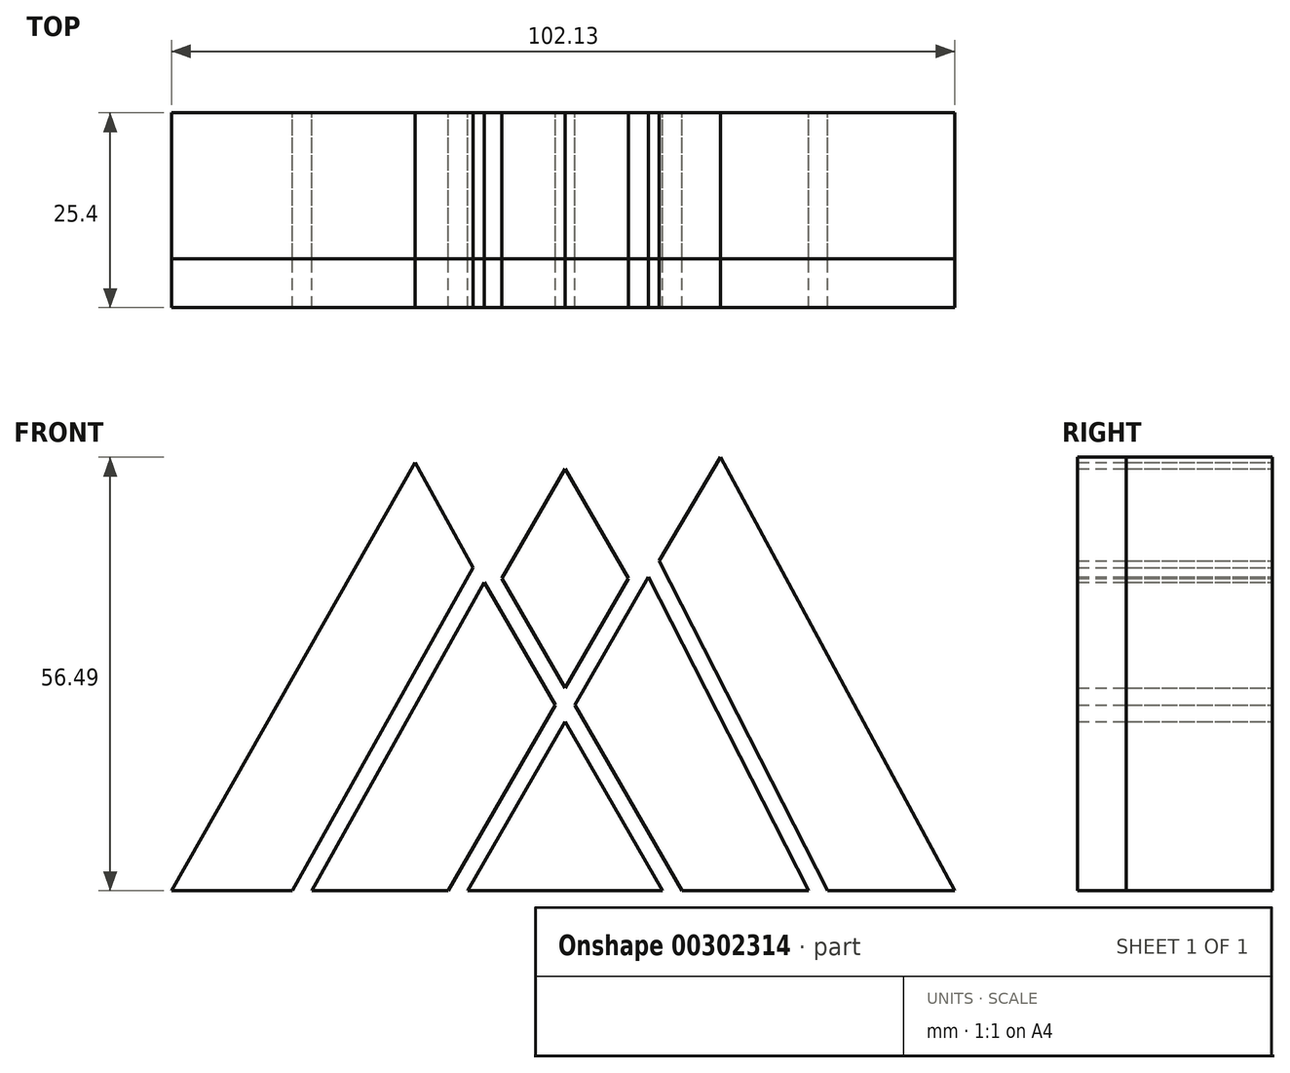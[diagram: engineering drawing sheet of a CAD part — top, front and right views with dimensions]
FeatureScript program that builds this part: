
annotation { "Feature Type Name" : "Feature", "Feature Type Description" : "" }
export const myFeature = defineFeature(function(context is Context, id is Id, definition is map)
    precondition{}
    {
        {
            var Q0;
            Q0=qCreatedBy(makeId("Front.planeOp"),FACE);
            var sketch = newSketch(context, id + "F0", { "sketchPlane" : qUnion([Q0])});
            skLineSegment(sketch, "E0", {"start": v(0, 0) * mm, "end": v(-12.7, -22) * mm});
            skLineSegment(sketch, "E1", {"start": v(0, 0) * mm, "end": v(12.7, -22) * mm});
            skLineSegment(sketch, "E2", {"start": v(-12.7, -22) * mm, "end": v(12.7, -22) * mm});
            skLineSegment(sketch, "E3", {"start": v(0, -22) * mm, "end": v(0, 0) * mm});
            skLineSegment(sketch, "E4", {"start": v(-19.53, 33.84) * mm, "end": v(-51.28, -22) * mm});
            skLineSegment(sketch, "E5", {"start": v(20.27, 34.5) * mm, "end": v(50.85, -22) * mm});
            skLineSegment(sketch, "E6", {"start": v(-11.95, 20.1) * mm, "end": v(-35.53, -22) * mm});
            skLineSegment(sketch, "E7", {"start": v(12.3, 21) * mm, "end": v(34.23, -22) * mm});
            skLineSegment(sketch, "E8", {"start": v(-1.27, 2.2) * mm, "end": v(-15.24, -22) * mm});
            skLineSegment(sketch, "E9", {"start": v(1.27, 2.2) * mm, "end": v(15.24, -22) * mm});
            skLineSegment(sketch, "E10", {"start": v(15.24, -22) * mm, "end": v(31.75, -22) * mm});
            skLineSegment(sketch, "E11", {"start": v(0, 33) * mm, "end": v(-8.26, 18.7) * mm});
            skLineSegment(sketch, "E12", {"start": v(-10.5, 18.18) * mm, "end": v(-33, -22) * mm});
            skLineSegment(sketch, "E13", {"start": v(0, 33) * mm, "end": v(8.25, 18.7) * mm});
            skLineSegment(sketch, "E14", {"start": v(10.9, 18.88) * mm, "end": v(31.75, -22) * mm});
            skLineSegment(sketch, "E15", {"start": v(-8.26, 18.7) * mm, "end": v(0, 4.4) * mm});
            skLineSegment(sketch, "E16", {"start": v(8.25, 18.7) * mm, "end": v(0, 4.4) * mm});
            skLineSegment(sketch, "E17", {"start": v(-10.5, 18.18) * mm, "end": v(-1.27, 2.2) * mm});
            skLineSegment(sketch, "E18", {"start": v(10.9, 18.88) * mm, "end": v(1.27, 2.2) * mm});
            skLineSegment(sketch, "E19", {"start": v(-19.53, 33.84) * mm, "end": v(-11.95, 20.1) * mm});
            skLineSegment(sketch, "E20", {"start": v(-51.28, -22) * mm, "end": v(-35.53, -22) * mm});
            skLineSegment(sketch, "E21", {"start": v(-33, -22) * mm, "end": v(-15.24, -22) * mm});
            skLineSegment(sketch, "E22", {"start": v(31.75, -22) * mm, "end": v(50.85, -22) * mm});
            skLineSegment(sketch, "E23", {"start": v(12.3, 21) * mm, "end": v(20.27, 34.5) * mm});
            skSolve(sketch);
        }
        {
            var Q0;
            Q0 = qSketchRegion(id + "F0", true);
            extrude(context, id + "F1", {"entities" : qUnion([Q0]), "depth" : 19.05 * mm});
        }
        {
            var Q0;
            Q0 = qSketchRegion(id + "F0", true);
            extrude(context, id + "F2", {"entities" : qUnion([Q0]), "depth" : 25.4 * mm});
        }
    });
